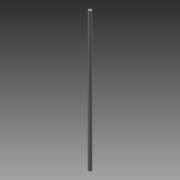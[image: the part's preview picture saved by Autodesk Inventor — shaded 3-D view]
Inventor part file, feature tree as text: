
AUTODESK INVENTOR PART (.ipt)
format: ipt  version: 2013 (Build 170138000, 138)  size: 68,096 bytes
history: native  units: in
note: dims shown in document units (in); Inventor stores cm internally (conversion verified against a paired STEP export)
features: extrude x1, sketch x1
ambient origin geometry x8: Origin, YZ Plane, XZ Plane, XY Plane, X Axis, Y Axis, Z Axis, Center Point
bodies: Solid1 (feature_tree)
feature tree (2):
  extrude  "Extrusion1"  Depth=20.0in TaperAngle=0.0deg
  sketch  "Sketch1"  dims[d0=0.5in d1=20.0in d2=0.0in]
